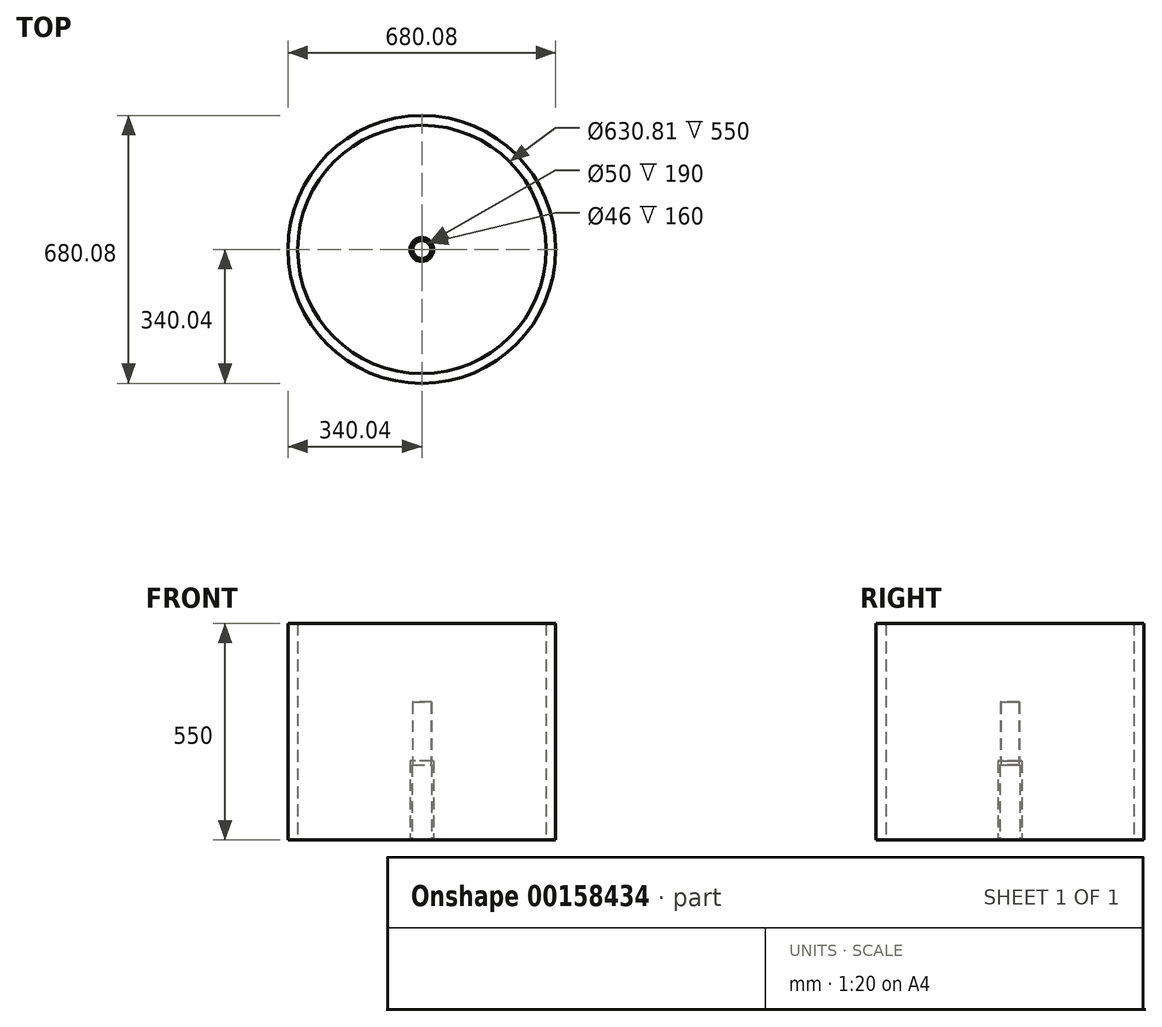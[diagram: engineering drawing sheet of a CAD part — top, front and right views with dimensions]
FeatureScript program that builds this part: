
annotation { "Feature Type Name" : "Feature", "Feature Type Description" : "" }
export const myFeature = defineFeature(function(context is Context, id is Id, definition is map)
    precondition{}
    {
        {
            var Q0;
            Q0=qCreatedBy(makeId("Top.planeOp"),FACE);
            var sketch = newSketch(context, id + "F0", { "sketchPlane" : qUnion([Q0])});
            skCircle(sketch, "E0", {"center": v(0, 0) * mm, "radius": 25 * mm});
            skCircle(sketch, "E1", {"center": v(0, 0) * mm, "radius": 30 * mm});
            skSolve(sketch);
        }
        {
            var Q0;
            Q0 = qSketchRegion(id + "F0", true);
            extrude(context, id + "F1", {"entities" : qUnion([Q0]), "depth" : 200 * mm});
        }
        {
            var Q0;
            Q0=makeQuery(id+"F1.opExtrude","CAP_FACE",FACE,{"disambiguationData":[OSD([sQuery(id+"F0.wireOp",EDGE,"E0"),sQuery(id+"F0.wireOp",EDGE,"E1")])],"isStart":false});
            var sketch = newSketch(context, id + "F2", { "sketchPlane" : qUnion([Q0])});
            skCircle(sketch, "E2", {"center": v(0, 0) * mm, "radius": 24 * mm});
            skCircle(sketch, "E3", {"center": v(0, 0) * mm, "radius": 30 * mm});
            skSolve(sketch);
        }
        {
            var Q0;
            Q0=qCreatedBy(makeId("Top.planeOp"),FACE);
            var sketch = newSketch(context, id + "F3", { "sketchPlane" : qUnion([Q0])});
            skCircle(sketch, "E4", {"center": v(0, 0) * mm, "radius": 340.04 * mm});
            skCircle(sketch, "E5", {"center": v(0, 0) * mm, "radius": 315.4 * mm});
            skSolve(sketch);
        }
        {
            var Q0;
            Q0=makeQuery(id+"F3.imprint","IMPRINT",FACE,{"disambiguationData":[TD([[makeQuery(id+"F3.imprint","IMPRINT",EDGE,{"derivedFrom":sQuery(id+"F3.wireOp",EDGE,"E4")}),1.0]])]});
            extrude(context, id + "F4", {"entities" : qUnion([Q0]), "depth" : 550 * mm});
        }
        {
            var Q0;
            Q0=makeQuery(id+"F2.imprint","IMPRINT",FACE,{"disambiguationData":[TD([[makeQuery(id+"F2.imprint","IMPRINT",EDGE,{"derivedFrom":sQuery(id+"F2.wireOp",EDGE,"E2")}),-1.0]])]});
            extrude(context, id + "F5", {"entities" : qUnion([Q0]), "operationType" : NewBodyOperationType.ADD, "oppositeDirection" : true, "depth" : 5 * mm});
        }
        {
            var Q0;
            Q0=makeQuery(id+"F5.opExtrude","CAP_FACE",FACE,{"disambiguationData":[OSD([sQuery(id+"F0.wireOp",EDGE,"E0"),sQuery(id+"F2.wireOp",EDGE,"E2")])],"isStart":false});
            var sketch = newSketch(context, id + "F6", { "sketchPlane" : qUnion([Q0])});
            skCircle(sketch, "E6", {"center": v(0, 0) * mm, "radius": 24 * mm});
            skCircle(sketch, "E7", {"center": v(0, 0) * mm, "radius": 25 * mm});
            skSolve(sketch);
        }
        {
            var Q0;
            Q0=makeQuery(id+"F6.imprint","IMPRINT",FACE,{"disambiguationData":[TD([[makeQuery(id+"F6.imprint","IMPRINT",EDGE,{"derivedFrom":sQuery(id+"F6.wireOp",EDGE,"E6")}),1.0]])]});
            extrude(context, id + "F7", {"entities" : qUnion([Q0]), "depth" : 5 * mm});
        }
        {
            var Q0;
            Q0=makeQuery(id+"F7.opExtrude","CAP_FACE",FACE,{"disambiguationData":[OSD([sQuery(id+"F6.wireOp",EDGE,"E6"),sQuery(id+"F6.wireOp",EDGE,"E7")])],"isStart":false});
            var sketch = newSketch(context, id + "F8", { "sketchPlane" : qUnion([Q0])});
            skCircle(sketch, "E8", {"center": v(0, 0) * mm, "radius": 23 * mm});
            skCircle(sketch, "E9", {"center": v(0, 0) * mm, "radius": 25 * mm});
            skSolve(sketch);
        }
        {
            var Q0;
            Q0=makeQuery(id+"F8.imprint","IMPRINT",FACE,{"disambiguationData":[TD([[makeQuery(id+"F8.imprint","IMPRINT",EDGE,{"derivedFrom":sQuery(id+"F8.wireOp",EDGE,"E8")}),-1.0]])]});
            extrude(context, id + "F9", {"entities" : qUnion([Q0]), "operationType" : NewBodyOperationType.ADD, "oppositeDirection" : true, "depth" : 160 * mm});
        }
    });
